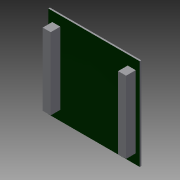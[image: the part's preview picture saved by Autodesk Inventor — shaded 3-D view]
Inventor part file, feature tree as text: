
AUTODESK INVENTOR PART (.ipt)
format: ipt  version: 2013 (Build 170138000, 138)  size: 111,616 bytes
history: native  units: in
note: dims shown in document units (in); Inventor stores cm internally (conversion verified against a paired STEP export)
features: extrude x2, sketch x2
ambient origin geometry x8: Origin, YZ Plane, XZ Plane, XY Plane, X Axis, Y Axis, Z Axis, Center Point
bodies: Solid1 (feature_tree)
feature tree (4):
  extrude  "Extrusion1"  Depth=2.25in
  extrude  "Extrusion4"  Depth=0.1in
  sketch  "Sketch1"  dims[d0=0.0394in d1=0.0in d2=2.25in]
  sketch  "Sketch4"  dims[d4=2.25in d21=0.1in d22=1.7717in d23=0.1969in d24=0.8858in d25=0.2362in d26=0.0in]
